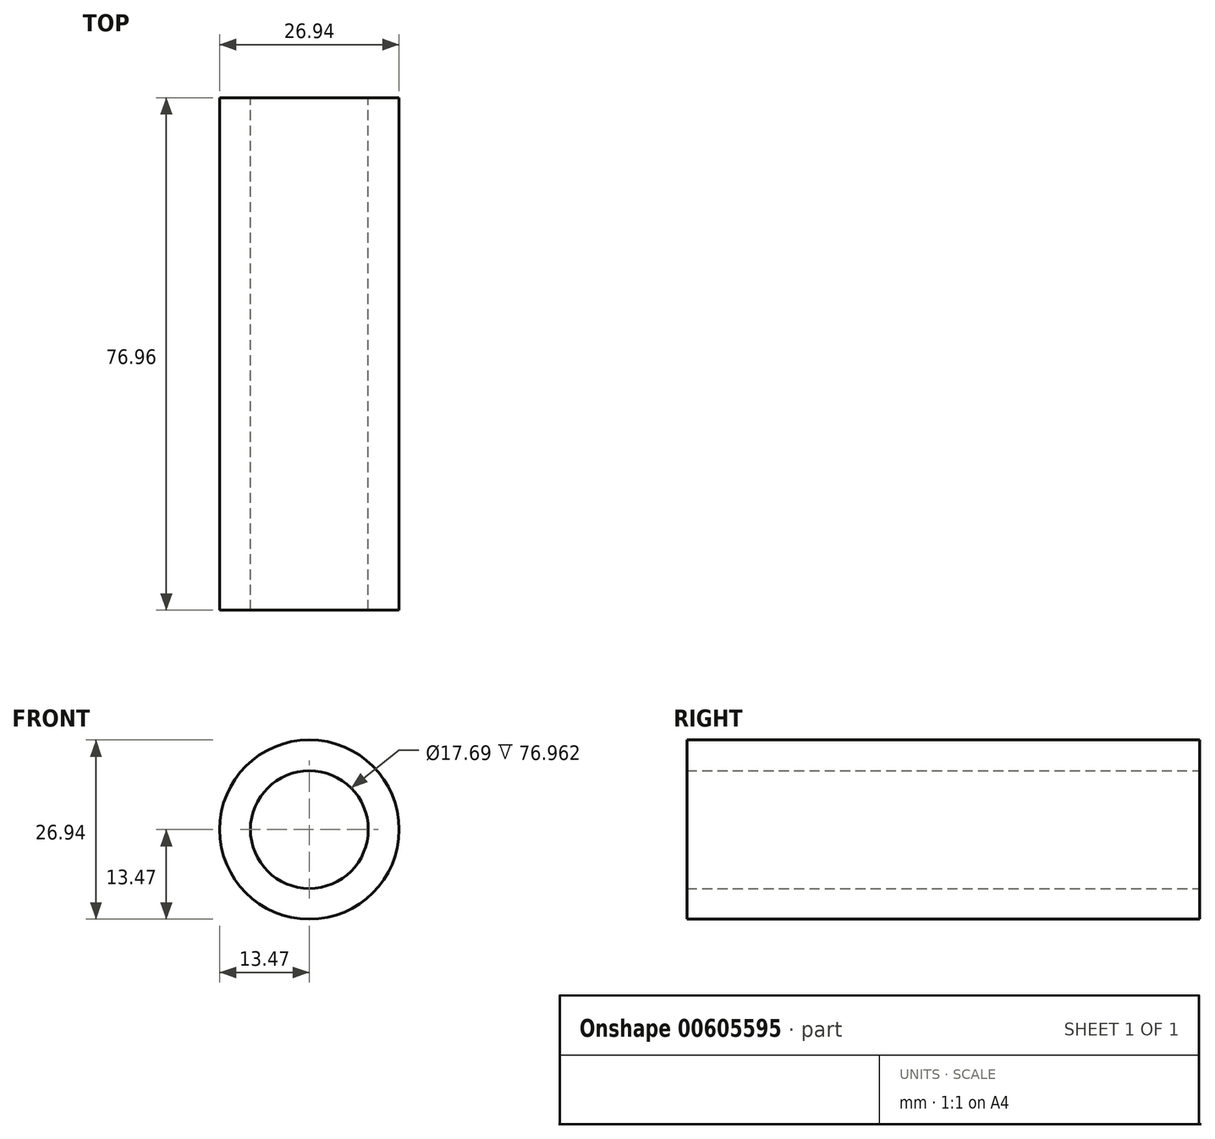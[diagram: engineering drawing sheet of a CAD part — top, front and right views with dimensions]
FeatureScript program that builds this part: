
annotation { "Feature Type Name" : "Feature", "Feature Type Description" : "" }
export const myFeature = defineFeature(function(context is Context, id is Id, definition is map)
    precondition{}
    {
        {
            var Q0;
            Q0=qCreatedBy(makeId("Front.planeOp"),FACE);
            var sketch = newSketch(context, id + "F0", { "sketchPlane" : qUnion([Q0])});
            skCircle(sketch, "E0", {"center": v(0, 0) * mm, "radius": 8.85 * mm});
            skCircle(sketch, "E1", {"center": v(0, 0) * mm, "radius": 13.47 * mm});
            skSolve(sketch);
        }
        {
            var Q0;
            Q0 = qSketchRegion(id + "F0", true);
            extrude(context, id + "F1", {"entities" : qUnion([Q0]), "depth" : 76.96 * mm, "offsetDistance" : 25.4 * mm});
        }
    });
